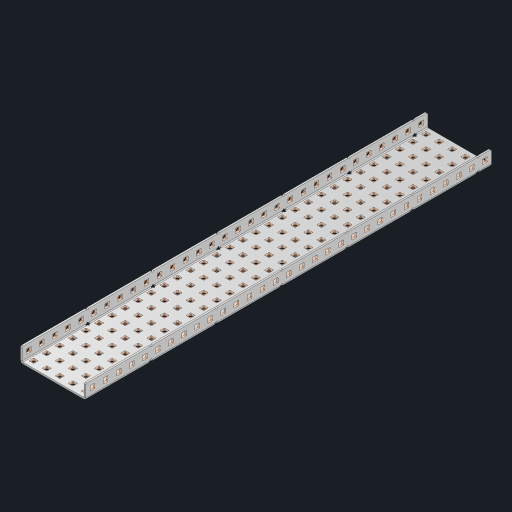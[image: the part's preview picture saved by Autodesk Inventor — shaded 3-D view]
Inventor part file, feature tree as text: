
AUTODESK INVENTOR PART (.ipt)
format: ipt  version: 2023 (Build 270158000, 158)  size: 2,318,848 bytes
history: native  units: in
note: dims shown in document units (in); Inventor stores cm internally (conversion verified against a paired STEP export)
features: other x222, extrude x216, sheet_metal_op x10, sketch x8, mirror x1, pattern_linear x1, chamfer x1
ambient origin geometry x8: Origin, YZ Plane, XZ Plane, XY Plane, X Axis, Y Axis, Z Axis, Center Point
bodies: Solid1 (feature_tree), Body (feature_tree)
feature tree (459):
  other  "Flange Pattern Plane"
  sheet_metal_op  "Flange Pattern"
  sheet_metal_op  "Body Pattern"
  other  "Arc Length"
  mirror  "Notch Mirror"
  pattern_linear  "Notch Pattern"  Spacing1=0.25in  [1 undecoded]
  chamfer  "End Chamfer"
  extrude  "Half Cut"  Depth=0.0625in
  sketch  "Sketch1"  dims[d0=2.5in]
  other  "Plate1"
  sketch  "Sketch2"  dims[d1=15.5in]
  other  "Plate2"
  sheet_metal_op  "Bend1"
  sheet_metal_op  "Corner1"
  sketch  "Sketch3"  dims[d2=0.0625in]
  other  "Flange Pattern Sketch"
  sketch  "Sketch7"  dims[d3=0.0625in]
  other  "Srf1"
  other  "Srf2"
  sketch  "Sketch8"  dims[d4=0.0312in]
  sketch  "Sketch9"  dims[d5=0.125in]
  other  "Srf91"
  sheet_metal_op  "Body Pattern Sketch"
  other  "Srf92"
  sketch  "Sketch13"  dims[d6=0.0625in]
  sketch  "Sketch14"  dims[d7=0.5in d8=90.0deg d9=0.0312in d10=0.25in d11=0.0625in d12=0.0625in d16=0.182in d17=0.02in d18=0.0625in d19=0.0in d20=0.25in d21=0.25in d46=0.172in d47=1.0in d48=0.0in d49=0.182in d50=0.02in d51=0.25in d52=0.25in d53=0.0625in d54=0.0in d55=0.172in d56=1.0in d57=0.0in d60=12.2047in d62=0.5in d63=1.9685in d65=0.5in d85=0.1473in d86=0.1782in d88=0.04in d89=0.0625in d90=0.0in d91=0.04in d92=0.0491in d95=2.5in d96=0.04in d97=0.25in d98=45.0deg d101=0.0in d102=2.497in d131=2.5in d132=12.2047in d134=0.5in d139=0.5in]
  other  "Srf856"
  other  "Srf1310"
  other  "Srf1311"
  other  "Srf1312"
  other  "Srf1376"
  other  "Srf1377"
  other  "Srf1728"
  other  "Srf1755"
  other  "Srf1878"
  other  "Srf1879"
  other  "Srf1880"
  other  "Srf1881"
  other  "Srf1882"
  other  "Srf1883"
  other  "Srf1884"
  other  "Srf1885"
  other  "Srf1886"
  other  "Srf1887"
  other  "Srf1888"
  other  "Srf1889"
  other  "Srf1890"
  other  "Srf1891"
  other  "Srf1892"
  other  "Srf1893"
  other  "Srf1894"
  other  "Srf1895"
  other  "Srf1896"
  other  "Srf1897"
  other  "Srf1898"
  other  "Srf1899"
  other  "Srf1900"
  other  "Srf1901"
  other  "Srf1902"
  other  "Srf1903"
  other  "Srf1904"
  other  "Srf1905"
  other  "Srf1906"
  other  "Srf1942"
  other  "Srf1943"
  other  "Srf1944"
  other  "Srf1945"
  other  "Srf1946"
  other  "Srf1947"
  other  "Srf1948"
  other  "Srf1949"
  other  "Srf1950"
  other  "Srf1951"
  other  "Srf1952"
  other  "Srf1953"
  other  "Srf1954"
  other  "Srf1955"
  other  "Srf1956"
  other  "Srf1957"
  other  "Srf1958"
  other  "Srf1959"
  other  "Srf1960"
  other  "Srf1961"
  other  "Srf1962"
  other  "Srf1963"
  other  "Srf1964"
  other  "Srf1965"
  other  "Srf1966"
  other  "Srf1967"
  other  "Srf1968"
  other  "Srf1969"
  other  "Srf1970"
  other  "Srf2111"
  other  "Srf2112"
  other  "Srf2113"
  other  "Srf2114"
  other  "Srf2115"
  other  "Srf2116"
  other  "Srf2117"
  other  "Srf2118"
  other  "Srf2119"
  other  "Srf2120"
  other  "Srf2121"
  other  "Srf2122"
  other  "Srf2123"
  other  "Srf2124"
  other  "Srf2125"
  other  "Srf2126"
  other  "Srf2127"
  other  "Srf2128"
  other  "Srf2129"
  other  "Srf2130"
  other  "Srf2131"
  other  "Srf2132"
  other  "Srf2133"
  other  "Srf2134"
  other  "Srf2135"
  other  "Srf2136"
  other  "Srf2137"
  other  "Srf2146"
  other  "Srf2147"
  other  "Srf2148"
  other  "Srf2149"
  other  "Srf2150"
  other  "Srf2151"
  other  "Srf2152"
  other  "Srf2153"
  other  "Srf2154"
  other  "Srf2155"
  other  "Srf2156"
  other  "Srf2157"
  other  "Srf2158"
  other  "Srf2159"
  other  "Srf2160"
  other  "Srf2161"
  other  "Srf2162"
  other  "Srf2163"
  other  "Srf2164"
  other  "Srf2165"
  other  "Srf2166"
  other  "Srf2167"
  other  "Srf2168"
  other  "Srf2169"
  other  "Srf2170"
  other  "Srf2171"
  other  "Srf2172"
  other  "Srf2173"
  other  "Srf2174"
  other  "Srf2175"
  other  "Srf2176"
  other  "Srf2177"
  other  "Srf2178"
  other  "Srf2179"
  other  "Srf2180"
  other  "Srf2181"
  other  "Srf2182"
  other  "Srf2183"
  other  "Srf2184"
  other  "Srf2185"
  other  "Srf2186"
  other  "Srf2187"
  other  "Srf2188"
  other  "Srf2189"
  other  "Srf2190"
  other  "Srf2191"
  other  "Srf2192"
  other  "Srf2193"
  other  "Srf2194"
  other  "Srf2195"
  other  "Srf2196"
  other  "Srf2197"
  other  "Srf2198"
  other  "Srf2199"
  other  "Srf2200"
  other  "Srf2201"
  other  "Srf2202"
  other  "Srf2203"
  other  "Srf2204"
  other  "Srf2205"
  other  "Srf2206"
  other  "Srf2207"
  other  "Srf2208"
  other  "Srf2209"
  other  "Srf2210"
  other  "Srf2211"
  other  "Srf2212"
  other  "Srf2213"
  other  "Srf2214"
  other  "Srf2215"
  other  "Srf2216"
  other  "Srf2217"
  other  "Srf2218"
  other  "Srf2219"
  other  "Srf2220"
  other  "Srf2221"
  other  "Srf2222"
  other  "Srf2223"
  other  "Srf2224"
  other  "Srf2225"
  other  "Srf2226"
  other  "Srf2227"
  other  "Srf2228"
  other  "Srf2229"
  other  "Srf2230"
  other  "Srf2231"
  other  "Srf2232"
  other  "Srf2233"
  other  "Srf2234"
  other  "Srf2235"
  other  "Srf2236"
  other  "Srf2237"
  other  "Srf2238"
  other  "Srf2239"
  other  "Srf2240"
  other  "Srf2241"
  other  "Srf2242"
  other  "Srf2243"
  other  "Srf2244"
  other  "Srf2245"
  other  "Srf2246"
  other  "Srf2247"
  other  "Srf2248"
  other  "Srf2249"
  other  "Srf2250"
  other  "Srf2251"
  other  "Srf2252"
  other  "Srf2253"
  other  "Srf2254"
  other  "Srf2255"
  other  "Srf2256"
  other  "Srf2257"
  other  "Srf2258"
  other  "Srf2259"
  other  "Srf2260"
  other  "Srf2261"
  other  "Srf2262"
  other  "Srf2263"
  other  "Srf2264"
  other  "Srf2265"
  sheet_metal_op  "Flange Stamp"
  sheet_metal_op  "Flange Circle"
  sheet_metal_op  "Body Stamp"
  sheet_metal_op  "Body Circle"
  sheet_metal_op  "Notch"
  extrude  "ExtrusionSrf2"  Depth=0.0625in
  extrude  "ExtrusionSrf92"  Depth=2.5in
  extrude  "ExtrusionSrf856"  Depth=0.02in
  extrude  "ExtrusionSrf1310"  Depth=0.0625in
  extrude  "ExtrusionSrf1311"  TaperAngle=0.0deg  [1 undecoded]
  extrude  "ExtrusionSrf1312"  Depth=0.25in
  extrude  "ExtrusionSrf1376"  Depth=0.25in
  extrude  "ExtrusionSrf1377"  Depth=2.5in
  extrude  "ExtrusionSrf1728"  Depth=2.5in TaperAngle=0.0deg
  extrude  "ExtrusionSrf1755"  Depth=2.5in
  extrude  "ExtrusionSrf1878"  Depth=0.02in
  extrude  "ExtrusionSrf1879"  Depth=0.25in
  extrude  "ExtrusionSrf1880"  Depth=0.25in
  extrude  "ExtrusionSrf1881"  Depth=0.0625in
  extrude  "ExtrusionSrf1882"  TaperAngle=0.0deg  [1 undecoded]
  extrude  "ExtrusionSrf1883"  Depth=2.5in
  extrude  "ExtrusionSrf1884"  Depth=2.5in TaperAngle=0.0deg
  extrude  "ExtrusionSrf1885"  Depth=2.5in
  extrude  "ExtrusionSrf1886"  Depth=2.5in
  extrude  "ExtrusionSrf1887"  Depth=2.5in
  extrude  "ExtrusionSrf1888"  Depth=2.5in
  extrude  "ExtrusionSrf1889"  Depth=2.5in
  extrude  "ExtrusionSrf1890"  Depth=0.0625in
  extrude  "ExtrusionSrf1891"  TaperAngle=0.0deg  [1 undecoded]
  extrude  "ExtrusionSrf1892"  Depth=2.5in
  extrude  "ExtrusionSrf1893"  Depth=2.5in
  extrude  "ExtrusionSrf1894"  Depth=2.5in
  extrude  "ExtrusionSrf1895"  Depth=0.25in TaperAngle=45.0deg
  extrude  "ExtrusionSrf1896"  TaperAngle=0.0deg  [1 undecoded]
  extrude  "ExtrusionSrf1897"  Depth=2.5in
  extrude  "ExtrusionSrf1898"  Depth=2.5in
  extrude  "ExtrusionSrf1899"  Depth=2.5in
  extrude  "ExtrusionSrf1900"  Depth=2.5in
  extrude  "ExtrusionSrf1901"  Depth=2.5in
  extrude  "ExtrusionSrf1902"  [1 undecoded]
  extrude  "ExtrusionSrf1903"  [1 undecoded]
  extrude  "ExtrusionSrf1904"  [1 undecoded]
  extrude  "ExtrusionSrf1905"  [1 undecoded]
  extrude  "ExtrusionSrf1906"  [1 undecoded]
  extrude  "ExtrusionSrf1942"  [1 undecoded]
  extrude  "ExtrusionSrf1943"  [1 undecoded]
  extrude  "ExtrusionSrf1944"  [1 undecoded]
  extrude  "ExtrusionSrf1945"  [1 undecoded]
  extrude  "ExtrusionSrf1946"  [1 undecoded]
  extrude  "ExtrusionSrf1947"  [1 undecoded]
  extrude  "ExtrusionSrf1948"  [1 undecoded]
  extrude  "ExtrusionSrf1949"  [1 undecoded]
  extrude  "ExtrusionSrf1950"  [1 undecoded]
  extrude  "ExtrusionSrf1951"  [1 undecoded]
  extrude  "ExtrusionSrf1952"  [1 undecoded]
  extrude  "ExtrusionSrf1953"  [1 undecoded]
  extrude  "ExtrusionSrf1954"  [1 undecoded]
  extrude  "ExtrusionSrf1955"  [1 undecoded]
  extrude  "ExtrusionSrf1956"  [1 undecoded]
  extrude  "ExtrusionSrf1957"  [1 undecoded]
  extrude  "ExtrusionSrf1958"  [1 undecoded]
  extrude  "ExtrusionSrf1959"  [1 undecoded]
  extrude  "ExtrusionSrf1960"  [1 undecoded]
  extrude  "ExtrusionSrf1961"  [1 undecoded]
  extrude  "ExtrusionSrf1962"  [1 undecoded]
  extrude  "ExtrusionSrf1963"  [1 undecoded]
  extrude  "ExtrusionSrf1964"  [1 undecoded]
  extrude  "ExtrusionSrf1965"  [1 undecoded]
  extrude  "ExtrusionSrf1966"  [1 undecoded]
  extrude  "ExtrusionSrf1967"  [1 undecoded]
  extrude  "ExtrusionSrf1968"  [1 undecoded]
  extrude  "ExtrusionSrf1969"  [1 undecoded]
  extrude  "ExtrusionSrf1970"  [1 undecoded]
  extrude  "ExtrusionSrf2111"  [1 undecoded]
  extrude  "ExtrusionSrf2112"  [1 undecoded]
  extrude  "ExtrusionSrf2113"  [1 undecoded]
  extrude  "ExtrusionSrf2114"  [1 undecoded]
  extrude  "ExtrusionSrf2115"  [1 undecoded]
  extrude  "ExtrusionSrf2116"  [1 undecoded]
  extrude  "ExtrusionSrf2117"  [1 undecoded]
  extrude  "ExtrusionSrf2118"  [1 undecoded]
  extrude  "ExtrusionSrf2119"  [1 undecoded]
  extrude  "ExtrusionSrf2120"  [1 undecoded]
  extrude  "ExtrusionSrf2121"  [1 undecoded]
  extrude  "ExtrusionSrf2122"  [1 undecoded]
  extrude  "ExtrusionSrf2123"  [1 undecoded]
  extrude  "ExtrusionSrf2124"  [1 undecoded]
  extrude  "ExtrusionSrf2125"  [1 undecoded]
  extrude  "ExtrusionSrf2126"  [1 undecoded]
  extrude  "ExtrusionSrf2127"  [1 undecoded]
  extrude  "ExtrusionSrf2128"  [1 undecoded]
  extrude  "ExtrusionSrf2129"  [1 undecoded]
  extrude  "ExtrusionSrf2130"  [1 undecoded]
  extrude  "ExtrusionSrf2131"  [1 undecoded]
  extrude  "ExtrusionSrf2132"  [1 undecoded]
  extrude  "ExtrusionSrf2133"  [1 undecoded]
  extrude  "ExtrusionSrf2134"  [1 undecoded]
  extrude  "ExtrusionSrf2135"  [1 undecoded]
  extrude  "ExtrusionSrf2136"  [1 undecoded]
  extrude  "ExtrusionSrf2137"  [1 undecoded]
  extrude  "ExtrusionSrf2146"  [1 undecoded]
  extrude  "ExtrusionSrf2147"  [1 undecoded]
  extrude  "ExtrusionSrf2148"  [1 undecoded]
  extrude  "ExtrusionSrf2149"  [1 undecoded]
  extrude  "ExtrusionSrf2150"  [1 undecoded]
  extrude  "ExtrusionSrf2151"  [1 undecoded]
  extrude  "ExtrusionSrf2152"  [1 undecoded]
  extrude  "ExtrusionSrf2153"  [1 undecoded]
  extrude  "ExtrusionSrf2154"  [1 undecoded]
  extrude  "ExtrusionSrf2155"  [1 undecoded]
  extrude  "ExtrusionSrf2156"  [1 undecoded]
  extrude  "ExtrusionSrf2157"  [1 undecoded]
  extrude  "ExtrusionSrf2158"  [1 undecoded]
  extrude  "ExtrusionSrf2159"  [1 undecoded]
  extrude  "ExtrusionSrf2160"  [1 undecoded]
  extrude  "ExtrusionSrf2161"  [1 undecoded]
  extrude  "ExtrusionSrf2162"  [1 undecoded]
  extrude  "ExtrusionSrf2163"  [1 undecoded]
  extrude  "ExtrusionSrf2164"  [1 undecoded]
  extrude  "ExtrusionSrf2165"  [1 undecoded]
  extrude  "ExtrusionSrf2166"  [1 undecoded]
  extrude  "ExtrusionSrf2167"  [1 undecoded]
  extrude  "ExtrusionSrf2168"  [1 undecoded]
  extrude  "ExtrusionSrf2169"  [1 undecoded]
  extrude  "ExtrusionSrf2170"  [1 undecoded]
  extrude  "ExtrusionSrf2171"  [1 undecoded]
  extrude  "ExtrusionSrf2172"  [1 undecoded]
  extrude  "ExtrusionSrf2173"  [1 undecoded]
  extrude  "ExtrusionSrf2174"  [1 undecoded]
  extrude  "ExtrusionSrf2175"  [1 undecoded]
  extrude  "ExtrusionSrf2176"  [1 undecoded]
  extrude  "ExtrusionSrf2177"  [1 undecoded]
  extrude  "ExtrusionSrf2178"  [1 undecoded]
  extrude  "ExtrusionSrf2179"  [1 undecoded]
  extrude  "ExtrusionSrf2180"  [1 undecoded]
  extrude  "ExtrusionSrf2181"  [1 undecoded]
  extrude  "ExtrusionSrf2182"  [1 undecoded]
  extrude  "ExtrusionSrf2183"  [1 undecoded]
  extrude  "ExtrusionSrf2184"  [1 undecoded]
  extrude  "ExtrusionSrf2185"  [1 undecoded]
  extrude  "ExtrusionSrf2186"  [1 undecoded]
  extrude  "ExtrusionSrf2187"  [1 undecoded]
  extrude  "ExtrusionSrf2188"  [1 undecoded]
  extrude  "ExtrusionSrf2189"  [1 undecoded]
  extrude  "ExtrusionSrf2190"  [1 undecoded]
  extrude  "ExtrusionSrf2191"  [1 undecoded]
  extrude  "ExtrusionSrf2192"  [1 undecoded]
  extrude  "ExtrusionSrf2193"  [1 undecoded]
  extrude  "ExtrusionSrf2194"  [1 undecoded]
  extrude  "ExtrusionSrf2195"  [1 undecoded]
  extrude  "ExtrusionSrf2196"  [1 undecoded]
  extrude  "ExtrusionSrf2197"  [1 undecoded]
  extrude  "ExtrusionSrf2198"  [1 undecoded]
  extrude  "ExtrusionSrf2199"  [1 undecoded]
  extrude  "ExtrusionSrf2200"  [1 undecoded]
  extrude  "ExtrusionSrf2201"  [1 undecoded]
  extrude  "ExtrusionSrf2202"  [1 undecoded]
  extrude  "ExtrusionSrf2203"  [1 undecoded]
  extrude  "ExtrusionSrf2204"  [1 undecoded]
  extrude  "ExtrusionSrf2205"  [1 undecoded]
  extrude  "ExtrusionSrf2206"  [1 undecoded]
  extrude  "ExtrusionSrf2207"  [1 undecoded]
  extrude  "ExtrusionSrf2208"  [1 undecoded]
  extrude  "ExtrusionSrf2209"  [1 undecoded]
  extrude  "ExtrusionSrf2210"  [1 undecoded]
  extrude  "ExtrusionSrf2211"  [1 undecoded]
  extrude  "ExtrusionSrf2212"  [1 undecoded]
  extrude  "ExtrusionSrf2213"  [1 undecoded]
  extrude  "ExtrusionSrf2214"  [1 undecoded]
  extrude  "ExtrusionSrf2215"  [1 undecoded]
  extrude  "ExtrusionSrf2216"  [1 undecoded]
  extrude  "ExtrusionSrf2217"  [1 undecoded]
  extrude  "ExtrusionSrf2218"  [1 undecoded]
  extrude  "ExtrusionSrf2219"  [1 undecoded]
  extrude  "ExtrusionSrf2220"  [1 undecoded]
  extrude  "ExtrusionSrf2221"  [1 undecoded]
  extrude  "ExtrusionSrf2222"  [1 undecoded]
  extrude  "ExtrusionSrf2223"  [1 undecoded]
  extrude  "ExtrusionSrf2224"  [1 undecoded]
  extrude  "ExtrusionSrf2225"  [1 undecoded]
  extrude  "ExtrusionSrf2226"  [1 undecoded]
  extrude  "ExtrusionSrf2227"  [1 undecoded]
  extrude  "ExtrusionSrf2228"  [1 undecoded]
  extrude  "ExtrusionSrf2229"  [1 undecoded]
  extrude  "ExtrusionSrf2230"  [1 undecoded]
  extrude  "ExtrusionSrf2231"  [1 undecoded]
  extrude  "ExtrusionSrf2232"  [1 undecoded]
  extrude  "ExtrusionSrf2233"  [1 undecoded]
  extrude  "ExtrusionSrf2234"  [1 undecoded]
  extrude  "ExtrusionSrf2235"  [1 undecoded]
  extrude  "ExtrusionSrf2236"  [1 undecoded]
  extrude  "ExtrusionSrf2237"  [1 undecoded]
  extrude  "ExtrusionSrf2238"  [1 undecoded]
  extrude  "ExtrusionSrf2239"  [1 undecoded]
  extrude  "ExtrusionSrf2240"  [1 undecoded]
  extrude  "ExtrusionSrf2241"  [1 undecoded]
  extrude  "ExtrusionSrf2242"  [1 undecoded]
  extrude  "ExtrusionSrf2243"  [1 undecoded]
  extrude  "ExtrusionSrf2244"  [1 undecoded]
  extrude  "ExtrusionSrf2245"  [1 undecoded]
  extrude  "ExtrusionSrf2246"  [1 undecoded]
  extrude  "ExtrusionSrf2247"  [1 undecoded]
  extrude  "ExtrusionSrf2248"  [1 undecoded]
  extrude  "ExtrusionSrf2249"  [1 undecoded]
  extrude  "ExtrusionSrf2250"  [1 undecoded]
  extrude  "ExtrusionSrf2251"  [1 undecoded]
  extrude  "ExtrusionSrf2252"  [1 undecoded]
  extrude  "ExtrusionSrf2253"  [1 undecoded]
  extrude  "ExtrusionSrf2254"  [1 undecoded]
  extrude  "ExtrusionSrf2255"  [1 undecoded]
  extrude  "ExtrusionSrf2256"  [1 undecoded]
  extrude  "ExtrusionSrf2257"  [1 undecoded]
  extrude  "ExtrusionSrf2258"  [1 undecoded]
  extrude  "ExtrusionSrf2259"  [1 undecoded]
  extrude  "ExtrusionSrf2260"  [1 undecoded]
  extrude  "ExtrusionSrf2261"  [1 undecoded]
  extrude  "ExtrusionSrf2262"  [1 undecoded]
  extrude  "ExtrusionSrf2263"  [1 undecoded]
  extrude  "ExtrusionSrf2264"  [1 undecoded]
  extrude  "ExtrusionSrf2265"  [1 undecoded]
note: 186 required parameter values undecoded (feature->parameter linkage not recoverable at this tier; creation-order binding heuristic only, values carry confidence <= 0.55)
